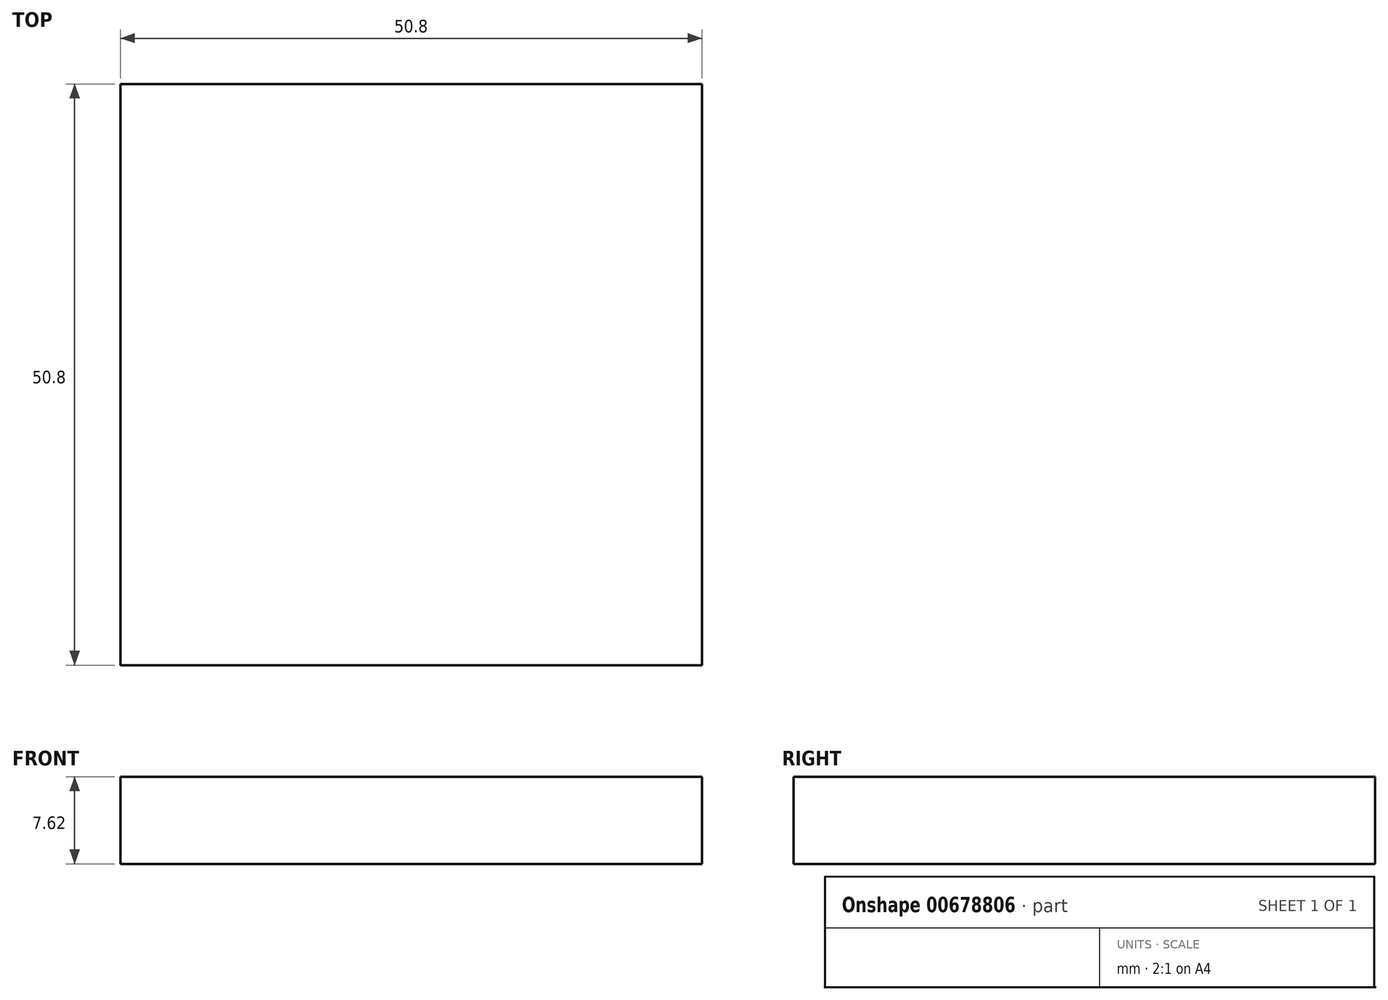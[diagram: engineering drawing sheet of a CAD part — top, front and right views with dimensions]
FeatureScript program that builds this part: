
annotation { "Feature Type Name" : "Feature", "Feature Type Description" : "" }
export const myFeature = defineFeature(function(context is Context, id is Id, definition is map)
    precondition{}
    {
        {
            var Q0;
            Q0=qCreatedBy(makeId("Top.planeOp"),FACE);
            var sketch = newSketch(context, id + "F0", { "sketchPlane" : qUnion([Q0])});
            skLineSegment(sketch, "E0", {"start": v(-37.64, 25.7) * mm, "end": v(-37.64, -25.1) * mm});
            skLineSegment(sketch, "E1", {"start": v(-37.64, -25.1) * mm, "end": v(13.16, -25.1) * mm});
            skLineSegment(sketch, "E2", {"start": v(13.16, -25.1) * mm, "end": v(13.16, 25.7) * mm});
            skLineSegment(sketch, "E3", {"start": v(13.16, 25.7) * mm, "end": v(-37.64, 25.7) * mm});
            skSolve(sketch);
        }
        {
            var Q0;
            Q0=makeQuery(id+"F0.imprint","IMPRINT",FACE,{"disambiguationData":[TD([[makeQuery(id+"F0.imprint","IMPRINT",EDGE,{"derivedFrom":sQuery(id+"F0.wireOp",EDGE,"E0")}),1.0]])]});
            extrude(context, id + "F1", {"entities" : qUnion([Q0]), "depth" : 7.62 * mm, "offsetDistance" : 25.4 * mm});
        }
    });
